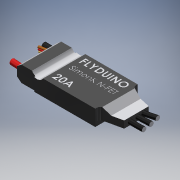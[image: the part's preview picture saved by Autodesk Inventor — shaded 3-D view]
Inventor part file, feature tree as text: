
AUTODESK INVENTOR PART (.ipt)
format: ipt  version: 2018 (Build 220112000, 112)  size: 747,520 bytes
history: native  units: mm
features: extrude x1, sketch x1, other x1
ambient origin geometry x8: Origin, YZ Plane, XZ Plane, XY Plane, X Axis, Y Axis, Z Axis, Center Point
bodies: Volumenkörper1 (feature_tree)
feature tree (3):
  extrude  "Extrusion1"  [1 undecoded]
  sketch  "Skizze1"  dims[d0=10.0mm d1=0.0mm]
  other  "Cut-Extrude4"
note: 1 required parameter value undecoded (feature->parameter linkage not recoverable at this tier; creation-order binding heuristic only, values carry confidence <= 0.55)
